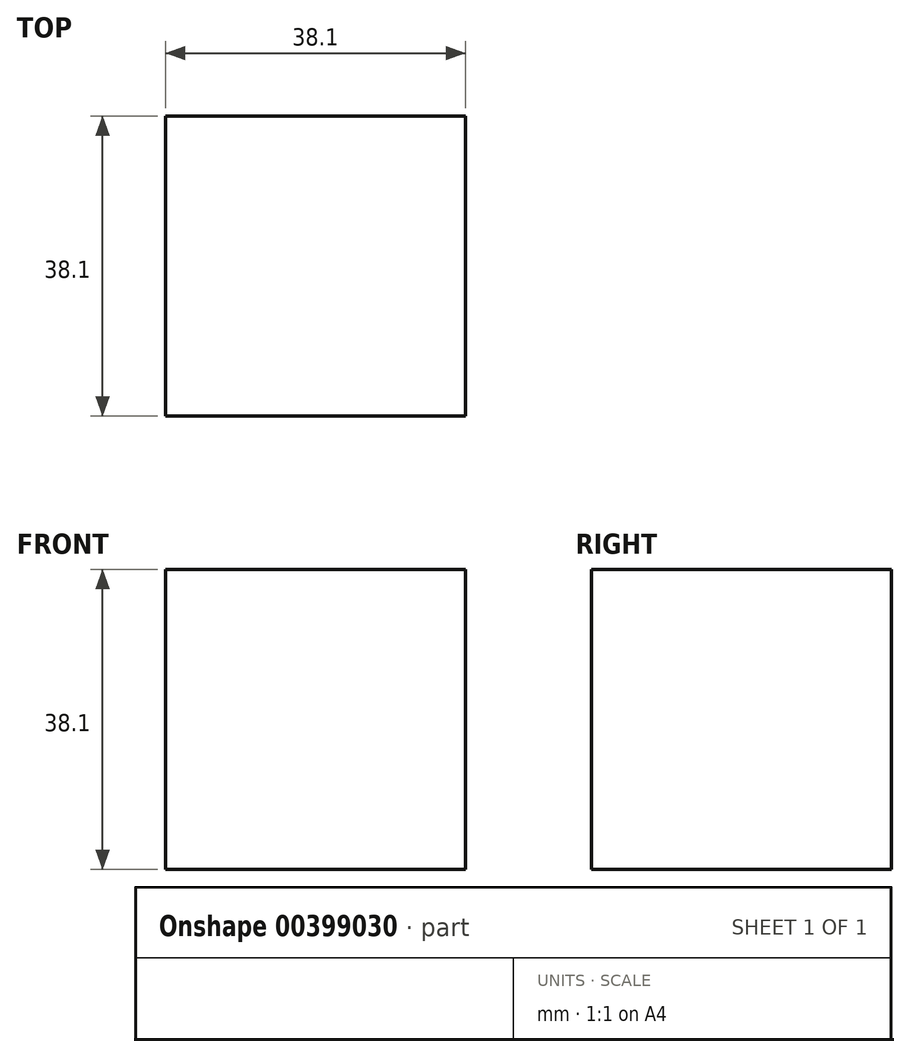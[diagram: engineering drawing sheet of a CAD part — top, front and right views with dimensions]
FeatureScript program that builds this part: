
annotation { "Feature Type Name" : "Feature", "Feature Type Description" : "" }
export const myFeature = defineFeature(function(context is Context, id is Id, definition is map)
    precondition{}
    {
        {
            var Q0;
            Q0=qCreatedBy(makeId("Top.planeOp"),FACE);
            var sketch = newSketch(context, id + "F0", { "sketchPlane" : qUnion([Q0])});
            skLineSegment(sketch, "E0.bottom", {"start": v(19.05, 19.05) * mm, "end": v(-19.05, 19.05) * mm});
            skLineSegment(sketch, "E0.top", {"start": v(19.05, -19.05) * mm, "end": v(-19.05, -19.05) * mm});
            skLineSegment(sketch, "E0.left", {"start": v(19.05, 19.05) * mm, "end": v(19.05, -19.05) * mm});
            skLineSegment(sketch, "E0.right", {"start": v(-19.05, 19.05) * mm, "end": v(-19.05, -19.05) * mm});
            skPoint(sketch, "E0.middle", {"position": v(0, 0) * mm});
            skSolve(sketch);
        }
        {
            var Q0;
            Q0 = qSketchRegion(id + "F0", true);
            extrude(context, id + "F1", {"entities" : qUnion([Q0]), "depth" : 38.1 * mm});
        }
    });
